# Revit family: Sanitary_Wash-basins_hansgrohe_63015XXX-Xuniva-Evo-E-Wash-bowl-650-400_SmartClean_HygieneEffect
name_source: partatom
category: Plumbing Fixtures
units: mm (PartAtom-declared; Revit-internal decimal feet)

## family parameters
Cut with Voids When Loaded = No
Host = Face
Maintain Annotation Orientation = No
OmniClass Number = 23.31.13.00
OmniClass Title = Sinks
Part Type = Normal
Room Calculation Point = No
Round Connector Dimension = Use Diameter
Shared = No

## types (1)
- 450 White
    Connector Description = Water Outlet 31.75mm
    Default Elevation = 1219 mm
    Description = Xuniva Evo E Wash bowl 650/400 without tap hole and overflow, SmartClean, HygieneEffect
    Diameter = 32 mm
    Manufacturer = Hansgrohe
    Material = Hansgrohe - Ceramic - 450 White
    Model = 63015XXX
    Product Page URL = https://www.hansgrohe.com
    Product data url = https://bimobject.com
    URL = https://www.hansgrohe.com
    Version = 1

## geometry (parser evidence)
native form markers: Sweep x2
no freeform markers — native parametric forms only
